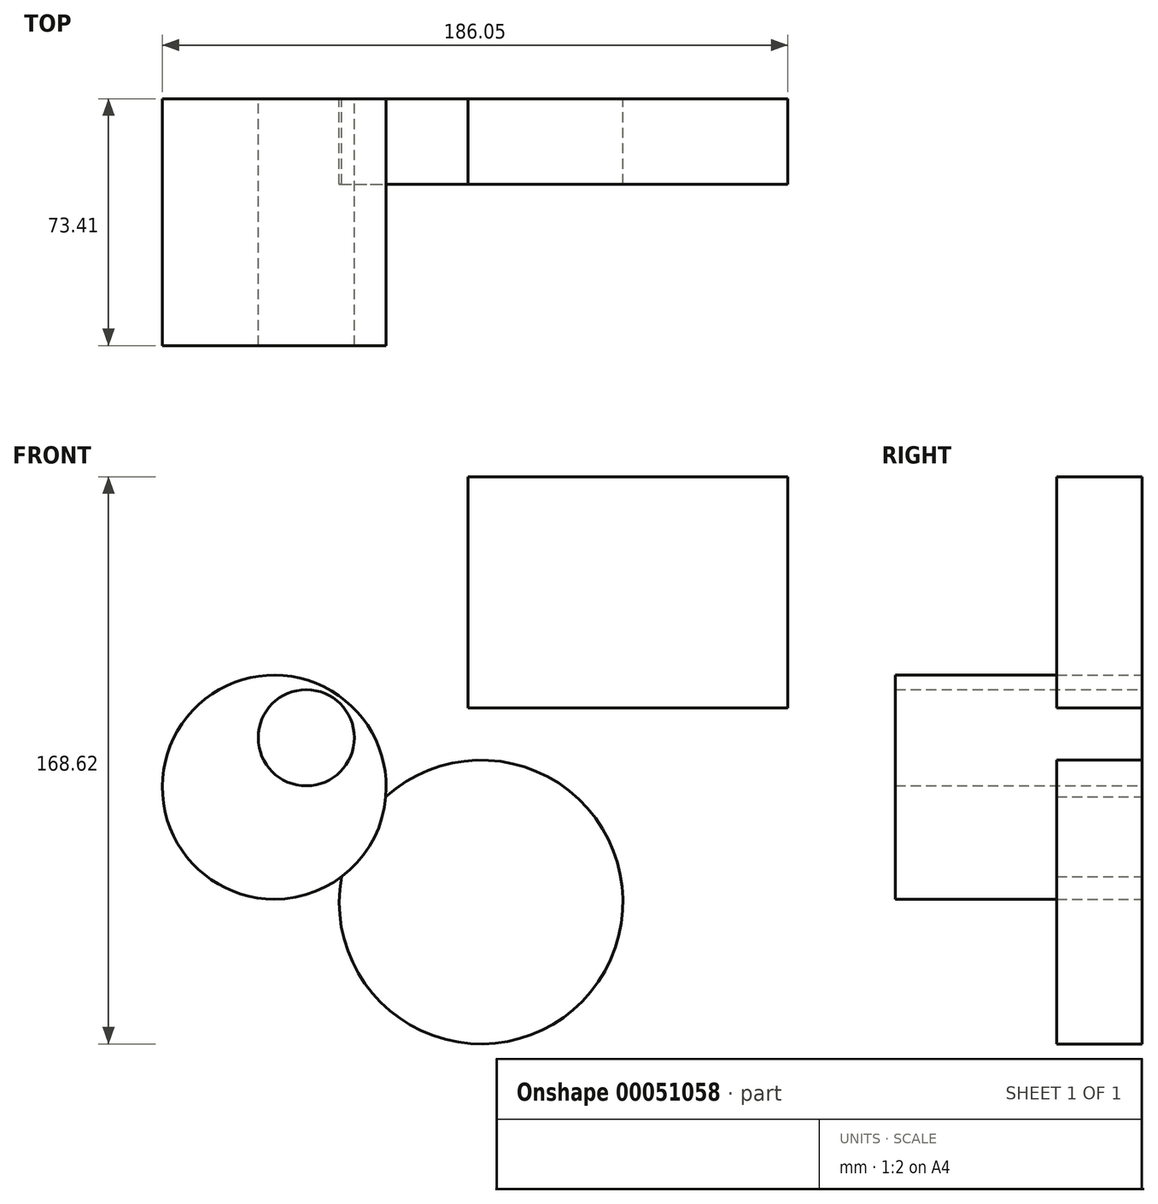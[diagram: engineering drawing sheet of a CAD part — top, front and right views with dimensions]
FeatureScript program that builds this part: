
annotation { "Feature Type Name" : "Feature", "Feature Type Description" : "" }
export const myFeature = defineFeature(function(context is Context, id is Id, definition is map)
    precondition{}
    {
        {
            var Q0;
            Q0=qCreatedBy(makeId("Front.planeOp"),FACE);
            var sketch = newSketch(context, id + "F0", { "sketchPlane" : qUnion([Q0])});
            skCircle(sketch, "E0", {"center": v(0, 0) * mm, "radius": 42.2 * mm});
            skLineSegment(sketch, "E1.bottom", {"start": v(-3.82, 57.7) * mm, "end": v(91.24, 57.7) * mm});
            skLineSegment(sketch, "E1.top", {"start": v(-3.82, 126.43) * mm, "end": v(91.24, 126.43) * mm});
            skLineSegment(sketch, "E1.left", {"start": v(-3.82, 57.7) * mm, "end": v(-3.82, 126.43) * mm});
            skLineSegment(sketch, "E1.right", {"start": v(91.24, 57.7) * mm, "end": v(91.24, 126.43) * mm});
            skLineSegment(sketch, "E2", {"start": v(0, 0) * mm, "end": v(0, 71.6) * mm, "construction": true});
            skSolve(sketch);
        }
        {
            var Q0;
            Q0=makeQuery(id+"F0.imprint","IMPRINT",FACE,{"disambiguationData":[TD([[makeQuery(id+"F0.imprint","IMPRINT",EDGE,{"derivedFrom":sQuery(id+"F0.wireOp",EDGE,"E1.bottom")}),1.0]])]});
            var Q1;
            Q1=makeQuery(id+"F0.imprint","IMPRINT",FACE,{"disambiguationData":[TD([[makeQuery(id+"F0.imprint","IMPRINT",EDGE,{"derivedFrom":sQuery(id+"F0.wireOp",EDGE,"E0")}),1.0]])]});
            extrude(context, id + "F1", {"entities" : qUnion([Q0, Q1]), "depth" : 25.4 * mm});
        }
        {
            var Q0;
            Q0=qCreatedBy(makeId("Front.planeOp"),FACE);
            var sketch = newSketch(context, id + "F2", { "sketchPlane" : qUnion([Q0])});
            skCircle(sketch, "E3", {"center": v(-61.5, 34.15) * mm, "radius": 33.3 * mm});
            skCircle(sketch, "E4", {"center": v(-52, 48.84) * mm, "radius": 14.3 * mm});
            skSolve(sketch);
        }
        {
            var Q0;
            Q0 = qSketchRegion(id + "F2", true);
            extrude(context, id + "F3", {"entities" : qUnion([Q0]), "operationType" : NewBodyOperationType.ADD, "depth" : 73.4 * mm, "offsetDistance" : 25.4 * mm});
        }
    });
